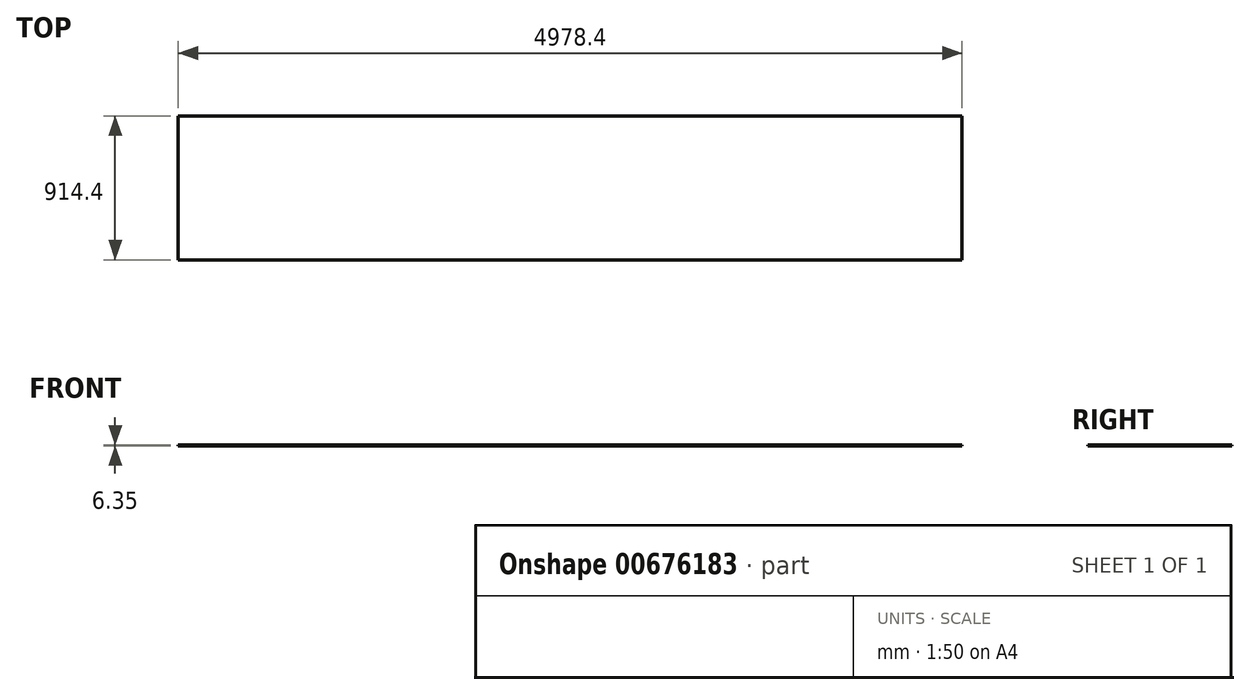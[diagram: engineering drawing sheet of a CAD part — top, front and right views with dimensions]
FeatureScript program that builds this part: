
annotation { "Feature Type Name" : "Feature", "Feature Type Description" : "" }
export const myFeature = defineFeature(function(context is Context, id is Id, definition is map)
    precondition{}
    {
        {
            var Q0;
            Q0=qCreatedBy(makeId("Top.planeOp"),FACE);
            var sketch = newSketch(context, id + "F0", { "sketchPlane" : qUnion([Q0])});
            skLineSegment(sketch, "E0.bottom", {"start": v(2489.2, -457.2) * mm, "end": v(-2489.2, -457.2) * mm});
            skLineSegment(sketch, "E0.top", {"start": v(2489.2, 457.2) * mm, "end": v(-2489.2, 457.2) * mm});
            skLineSegment(sketch, "E0.left", {"start": v(2489.2, -457.2) * mm, "end": v(2489.2, 457.2) * mm});
            skLineSegment(sketch, "E0.right", {"start": v(-2489.2, -457.2) * mm, "end": v(-2489.2, 457.2) * mm});
            skPoint(sketch, "E0.middle", {"position": v(0, 0) * mm});
            skSolve(sketch);
        }
        {
            var Q0;
            Q0=makeQuery(id+"F0.imprint","IMPRINT",FACE,{"disambiguationData":[TD([[makeQuery(id+"F0.imprint","IMPRINT",EDGE,{"derivedFrom":sQuery(id+"F0.wireOp",EDGE,"E0.bottom")}),-1.0]])]});
            extrude(context, id + "F1", {"entities" : qUnion([Q0]), "depth" : 6.35 * mm, "offsetDistance" : 25.4 * mm});
        }
    });
